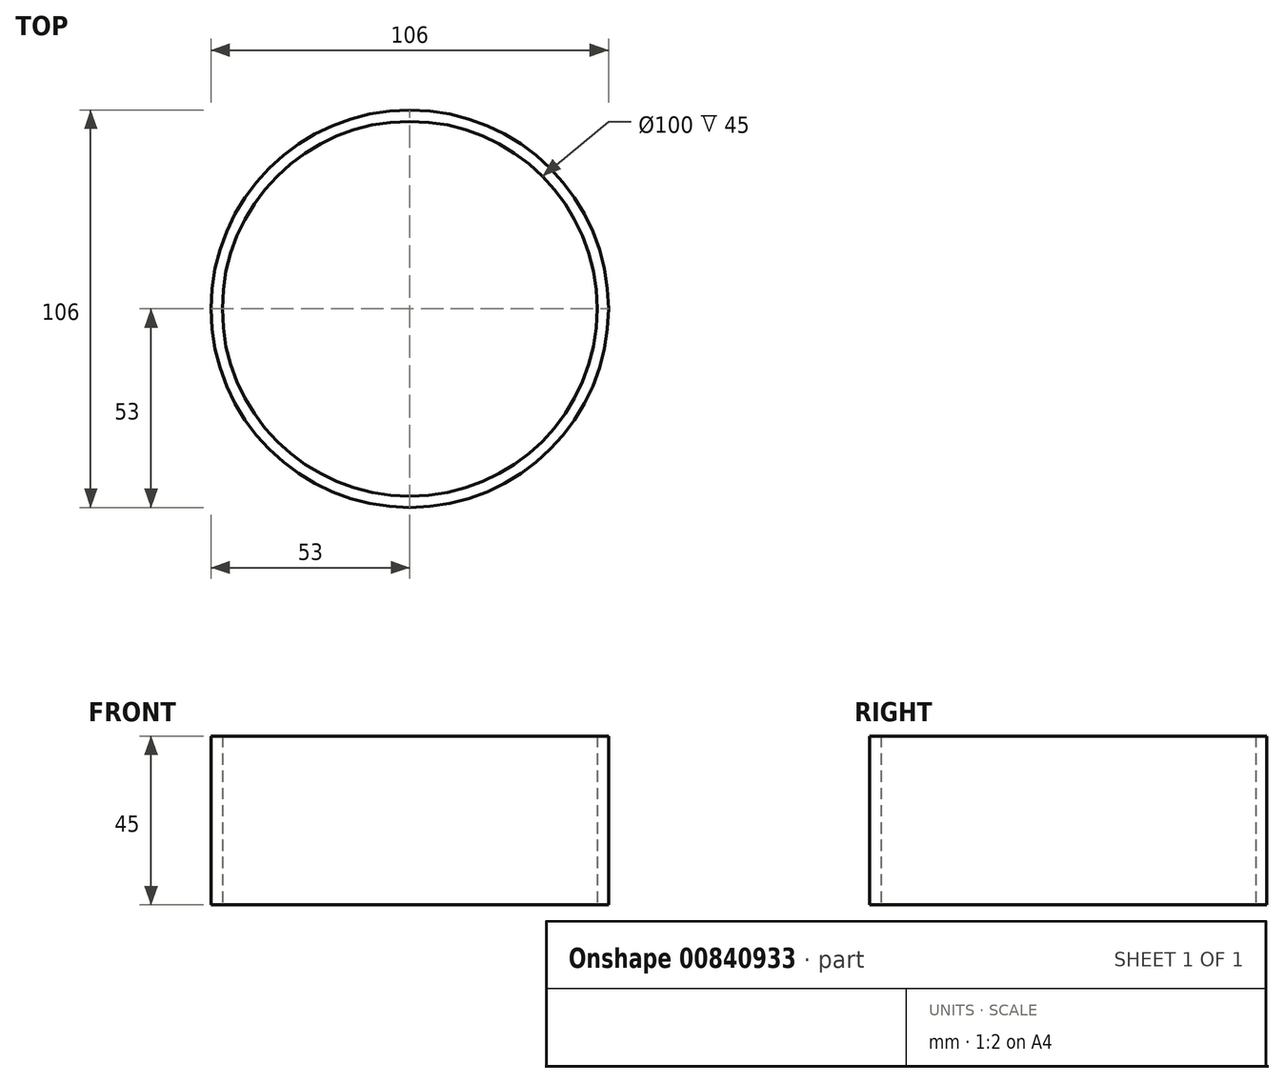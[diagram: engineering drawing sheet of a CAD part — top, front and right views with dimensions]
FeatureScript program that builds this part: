
annotation { "Feature Type Name" : "Feature", "Feature Type Description" : "" }
export const myFeature = defineFeature(function(context is Context, id is Id, definition is map)
    precondition{}
    {
        {
            var Q0;
            Q0=qCreatedBy(makeId("Top.planeOp"),FACE);
            var sketch = newSketch(context, id + "F0", { "sketchPlane" : qUnion([Q0])});
            skCircle(sketch, "E0", {"center": v(0, 0) * mm, "radius": 53 * mm});
            skCircle(sketch, "E1", {"center": v(0, 0) * mm, "radius": 50 * mm});
            skLineSegment(sketch, "E2", {"start": v(0, 50) * mm, "end": v(0, -50) * mm, "construction": true});
            skLineSegment(sketch, "E3", {"start": v(0, 0) * mm, "end": v(-50, 0) * mm, "construction": true});
            skLineSegment(sketch, "E4", {"start": v(0, 0) * mm, "end": v(50, 0) * mm, "construction": true});
            skSolve(sketch);
        }
        {
            var Q0;
            Q0=makeQuery(id+"F0.imprint","IMPRINT",FACE,{"disambiguationData":[TD([[makeQuery(id+"F0.imprint","IMPRINT",EDGE,{"derivedFrom":sQuery(id+"F0.wireOp",EDGE,"E0")}),1.0]])]});
            extrude(context, id + "F1", {"entities" : qUnion([Q0]), "depth" : 45 * mm, "offsetDistance" : 25 * mm});
        }
    });
